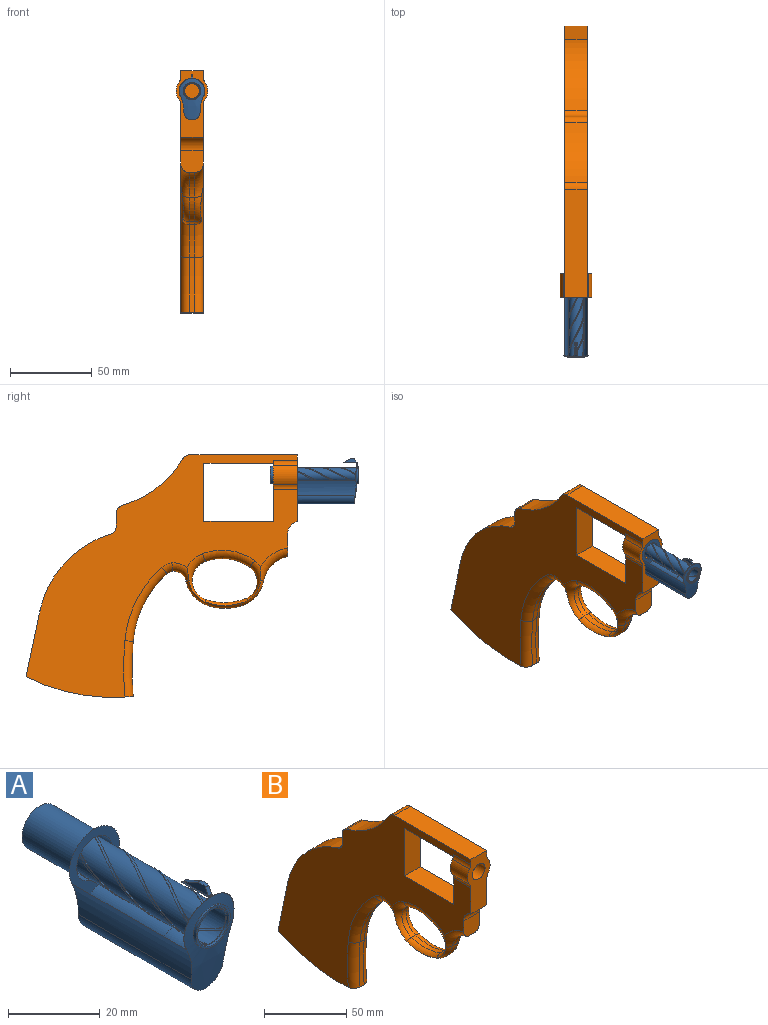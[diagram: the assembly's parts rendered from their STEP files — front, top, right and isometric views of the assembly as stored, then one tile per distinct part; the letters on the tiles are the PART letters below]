
ASSEMBLY  parts=2 mates=1
PART A: 49 faces, bbox 16.9x54.2x28.6 mm
  f0: cylinder r=4.95mm len=34.87mm, axis (0,1,0), area 458.1mm2, adj f1,f2,f3,f8,f45,f47
  f1: cylinder r=20.48mm len=35.45mm, axis (0,1,0), area 193.1mm2, adj f0,f2,f3,f9,f45,f46
  f2: plane 25.4x15.49mm, normal (0,1,0), area 144.5mm2, adj f0,f1,f8,f9,f10,f46,f47,f48
  f3: bspline ~27.83x16.8mm, area 209.2mm2, adj f0,f1,f8,f9,f29
  f4: cylinder r=4.51mm len=53.01mm, axis (0,1,0), area 266.9mm2, adj f11,f23,f25,f28
  f5: cylinder r=4.51mm len=53.05mm, axis (0,1,0), area 267mm2, adj f11,f14,f22,f28
  f6: cylinder r=4.51mm len=53.03mm, axis (0,1,0), area 266.9mm2, adj f11,f13,f19,f28
  f7: cylinder r=4.51mm len=53.2mm, axis (0,1,0), area 267.6mm2, adj f11,f16,f26,f28
  f8: cylinder r=20.48mm len=35.45mm, axis (0,1,0), area 336mm2, adj f0,f2,f3,f9
  f9: cylinder r=7.75mm len=35.91mm, axis (0,1,0), area 1097.4mm2, adj f1,f2,f3,f8,f40,f41,f42,f43
  f10: cylinder r=5.46mm len=16.89mm, axis (0,-1,0), area 579.6mm2, adj f2,f11
  f11: plane 10.92x10.92mm, normal (0,1,0), area 29.3mm2, adj f4,f5,f6,f7,f10,f12,f13,f14
  f12: cylinder r=4.51mm len=53.18mm, axis (0,1,0), area 267.2mm2, adj f11,f17,f20,f34
  f13: bspline ~53.03x9.38mm, area 11.1mm2, adj f6,f11,f15,f28
  f14: bspline ~53.21x9.63mm, area 11.3mm2, adj f5,f11,f15,f28
  f15: bspline ~53.21x9.63mm, area 33.3mm2, adj f11,f13,f14,f28
  f16: bspline ~53.2x9.38mm, area 11.1mm2, adj f7,f11,f18,f28
  f17: bspline ~53.18x9.39mm, area 11.3mm2, adj f11,f12,f18,f28
  f18: bspline ~53.21x9.62mm, area 33.4mm2, adj f11,f16,f17,f28
  f19: bspline ~53.21x9.61mm, area 11.3mm2, adj f6,f11,f21,f28
  f20: bspline ~53.21x9.61mm, area 10.7mm2, adj f11,f12,f21,f28
  f21: bspline ~53.21x9.61mm, area 33.2mm2, adj f11,f19,f20,f28
  f22: bspline ~52.96x9.38mm, area 11.1mm2, adj f5,f11,f24,f28
  f23: bspline ~53.21x9.58mm, area 11.3mm2, adj f4,f11,f24,f28
  f24: bspline ~53.21x9.62mm, area 33.2mm2, adj f11,f22,f23,f28
  f25: bspline ~53.21x9.57mm, area 11.1mm2, adj f4,f11,f27,f28
  f26: bspline ~53.05x9.39mm, area 11.3mm2, adj f7,f11,f27,f28
  f27: bspline ~53.21x9.63mm, area 33.3mm2, adj f11,f25,f26,f28
  f28: bspline ~27.83x16.8mm, area 6.4mm2, adj f4,f5,f6,f7,f13,f14,f15,f16
  f29: cylinder r=5.3mm len=10.61mm, axis (0,-1,0), area 19.7mm2, adj f3,f33
  f30: cylinder r=4.8mm len=9.59mm, axis (0,-1,0), area 17.8mm2, adj f28,f31,f32,f33,f34
  f31: bspline ~2.22x1.32mm, area 0mm2, adj f28,f30,f34
  f32: bspline ~2.22x1.33mm, area 0mm2, adj f28,f30,f34
  f33: plane 10.61x10.61mm, normal (0,-1,0), area 16.1mm2, adj f29,f30
  f34: bspline ~4.21x3.3mm, area 1.5mm2, adj f12,f30,f31,f32
  f35: plane 7.53x2.17mm, normal (1,0,0), area 10mm2, adj f37,f38,f39,f43,f44
  f36: plane 7.53x2.17mm, normal (-1,0,0), area 10mm2, adj f37,f38,f39,f40,f44
  f37: plane 4.71x2.17mm, normal (0,0.41,0.91), area 5.2mm2, adj f35,f36,f38,f40,f41,f43
  f38: cylinder r=3.04mm len=2.41mm, axis (-1,0,0), area 2.5mm2, adj f35,f36,f37,f44
  f39: plane 1.89x1.04mm, normal (0,-0.92,0.4), area 2.1mm2, adj f35,f36,f40,f42,f43,f44
  f40: cylinder r=0.23mm len=8.33mm, axis (0,1,0), area 2.7mm2, adj f9,f36,f37,f39,f41,f42
  f41: bspline ~1.47x0.17mm, area 0.1mm2, adj f9,f37,f40,f43
  f42: bspline ~1.47x0.22mm, area 0.3mm2, adj f9,f39,f40,f43
  f43: cylinder r=0.23mm len=8.33mm, axis (0,1,0), area 2.7mm2, adj f9,f35,f37,f39,f41,f42
  f44: cylinder r=0.23mm len=1.02mm, axis (-1,0,0), area 0.2mm2, adj f35,f36,f38,f39
  f45: torus R=5.42mm, axis (0,0,1), area 121.5mm2, adj f0,f1,f46,f47,f48
  f46: plane 28.08x3.95mm, normal (0,0,-1), area 105.5mm2, adj f1,f2,f45,f48
  f47: plane 27.5x2.62mm, normal (0,0,1), area 68.4mm2, adj f0,f2,f45,f48
  f48: cylinder r=3.81mm len=22.86mm, axis (0,-1,0), area 273.6mm2, adj f2,f45,f46,f47
PART B: 62 faces, bbox 19.7x166x148.5 mm
  f0: cylinder r=194.7mm len=33.52mm, axis (-1,0,0), area 119.4mm2, adj f1,f17,f49,f61
  f1: cylinder r=117.52mm len=65.41mm, axis (-1,0,0), area 913.4mm2, adj f0,f2,f18,f19,f49,f61
  f2: plane 39.56x13.72mm, normal (0,0.98,0.21), area 554.5mm2, adj f1,f3,f18,f19
  f3: cylinder r=96.75mm len=13.72mm, axis (-1,0,0), area 14.5mm2, adj f2,f4,f18,f19
  f4: cylinder r=62.89mm len=46.54mm, axis (-1,0,0), area 911.5mm2, adj f3,f18,f19,f35
  f5: plane 13.72x7.83mm, normal (0,1,0), area 107.4mm2, adj f18,f19,f35,f36
  f6: cylinder r=63.35mm len=36.83mm, axis (-1,0,0), area 652.6mm2, adj f18,f19,f36,f37
  f7: plane 65.63x13.72mm, normal (0,0,1), area 900.1mm2, adj f8,f18,f19,f37
  f8: plane 40.64x19.35mm, normal (0,-1,0), area 518.1mm2, adj f7,f9,f18,f19,f24,f25,f26,f27
  f9: cylinder r=7.75mm len=13.72mm, axis (-1,0,0), area 150.3mm2, adj f8,f10,f18,f19
  f10: plane 14.03x13.72mm, normal (0,-1,0), area 172.6mm2, adj f9,f11,f18,f19,f38,f50
  f11: cylinder r=19.07mm len=15.02mm, axis (-1,0,0), area 78.9mm2, adj f10,f12,f38,f50
  f12: cylinder r=19.74mm len=15.07mm, axis (-1,0,0), area 75.2mm2, adj f11,f13,f39,f52
  f13: cylinder r=33.56mm len=20.43mm, axis (-1,0,0), area 73.8mm2, adj f12,f14,f41,f55
  f14: cylinder r=20.11mm len=15.07mm, axis (-1,0,0), area 75.6mm2, adj f13,f15,f44,f57
  f15: cylinder r=7.61mm len=8.17mm, axis (-1,0,0), area 39.5mm2, adj f14,f16,f46,f58
  f16: cylinder r=5.84mm len=3.56mm, axis (-1,0,0), area 13.1mm2, adj f15,f17,f47,f59
  f17: cylinder r=62.53mm len=41.34mm, axis (-1,0,0), area 168.5mm2, adj f0,f16,f48,f60
  f18: plane 165.7x148.08mm, normal (1,0,0), area 9121mm2, adj f1,f2,f3,f4,f5,f6,f7,f8
  f19: plane 165.7x148.08mm, normal (-1,0,0), area 9121mm2, adj f1,f2,f3,f4,f5,f6,f7,f8
  f20: plane 37.06x19.35mm, normal (0,1,0), area 446.7mm2, adj f18,f19,f21,f23,f24,f25,f26,f27
  f21: plane 42.34x13.72mm, normal (0,0,1), area 580.8mm2, adj f18,f19,f20,f22
  f22: plane 35.43x13.72mm, normal (0,-1,0), area 486mm2, adj f18,f19,f21,f23
  f23: plane 42.34x13.72mm, normal (0,0,-1), area 580.8mm2, adj f18,f19,f20,f22
  f24: cylinder r=9.68mm len=14.73mm, axis (0,-1,0), area 179.1mm2, adj f8,f20,f28,f29
  f25: cylinder r=9.68mm len=14.73mm, axis (0,-1,0), area 179.1mm2, adj f8,f20,f26,f27
  f26: cylinder r=5.08mm len=14.73mm, axis (0,-1,0), area 47mm2, adj f8,f18,f20,f25
  f27: cylinder r=5.08mm len=14.73mm, axis (0,-1,0), area 47mm2, adj f8,f18,f20,f25
  f28: cylinder r=5.08mm len=14.73mm, axis (0,-1,0), area 47mm2, adj f8,f19,f20,f24
  f29: cylinder r=5.08mm len=14.73mm, axis (0,-1,0), area 47mm2, adj f8,f19,f20,f24
  f30: cylinder r=5.46mm len=14.73mm, axis (0,-1,0), area 505.5mm2, adj f8,f20
  f31: cylinder r=34.51mm len=24.89mm, axis (1,0,0), area 90.6mm2, adj f32,f34,f42,f54
  f32: cylinder r=12.36mm len=23.27mm, axis (1,0,0), area 107.8mm2, adj f31,f33,f45,f56
  f33: cylinder r=29.31mm len=27.13mm, axis (1,0,0), area 101.3mm2, adj f32,f34,f43,f53
  f34: cylinder r=10.83mm len=18.78mm, axis (1,0,0), area 81.6mm2, adj f31,f33,f40,f51
  f35: cylinder r=5.08mm len=13.72mm, axis (-1,0,0), area 88.8mm2, adj f4,f5,f18,f19
  f36: cylinder r=5.08mm len=13.72mm, axis (-1,0,0), area 89.9mm2, adj f5,f6,f18,f19
  f37: cylinder r=5.08mm len=13.72mm, axis (-1,0,0), area 71.9mm2, adj f6,f7,f18,f19
  f38: torus R=24.15mm, axis (1,0,0), area 181.3mm2, adj f10,f11,f18,f39,f40
  f39: torus R=14.66mm, axis (1,0,0), area 82.6mm2, adj f12,f38,f40,f41,f42
  f40: torus R=15.91mm, axis (1,0,0), area 127.7mm2, adj f18,f34,f38,f39,f42,f43
  f41: torus R=28.48mm, axis (1,0,0), area 87.9mm2, adj f13,f39,f42,f44
  f42: torus R=39.59mm, axis (1,0,0), area 110.4mm2, adj f31,f39,f40,f41,f44,f45
  f43: torus R=34.39mm, axis (1,0,0), area 241.5mm2, adj f18,f33,f40,f45
  f44: torus R=15.03mm, axis (1,0,0), area 82.5mm2, adj f14,f41,f42,f45,f46
  f45: torus R=17.44mm, axis (1,0,0), area 184.7mm2, adj f18,f32,f42,f43,f44,f46
  f46: torus R=12.69mm, axis (1,0,0), area 93.3mm2, adj f15,f18,f44,f45,f47
  f47: torus R=10.92mm, axis (1,0,0), area 38.7mm2, adj f16,f18,f46,f48
  f48: torus R=67.61mm, axis (1,0,0), area 389.2mm2, adj f17,f18,f47,f49
  f49: torus R=199.78mm, axis (1,0,0), area 270.4mm2, adj f0,f1,f18,f48
  f50: torus R=24.15mm, axis (1,0,0), area 181.3mm2, adj f10,f11,f19,f51,f52
  f51: torus R=15.91mm, axis (1,0,0), area 127.7mm2, adj f19,f34,f50,f52,f53,f54
  f52: torus R=14.66mm, axis (1,0,0), area 82.6mm2, adj f12,f50,f51,f54,f55
  f53: torus R=34.39mm, axis (1,0,0), area 241.5mm2, adj f19,f33,f51,f56
  f54: torus R=39.59mm, axis (1,0,0), area 110.4mm2, adj f31,f51,f52,f55,f56,f57
  f55: torus R=28.48mm, axis (1,0,0), area 87.9mm2, adj f13,f52,f54,f57
  f56: torus R=17.44mm, axis (1,0,0), area 184.7mm2, adj f19,f32,f53,f54,f57,f58
  f57: torus R=15.03mm, axis (1,0,0), area 82.5mm2, adj f14,f54,f55,f56,f58
  f58: torus R=12.69mm, axis (1,0,0), area 93.3mm2, adj f15,f19,f56,f57,f59
  f59: torus R=10.92mm, axis (1,0,0), area 38.7mm2, adj f16,f19,f58,f60
  f60: torus R=67.61mm, axis (1,0,0), area 389.2mm2, adj f17,f19,f59,f61
  f61: torus R=199.78mm, axis (1,0,0), area 270.4mm2, adj f0,f1,f19,f60
PLACE A t=(-31.77,-74.78,65.24)mm
PLACE B t=(-38.62,-30,61.67)mm
MATE cylindrical A.f4 <-> B.f30  axis (0,-1,0) through (-31.77,-57.89,87.09)mm
